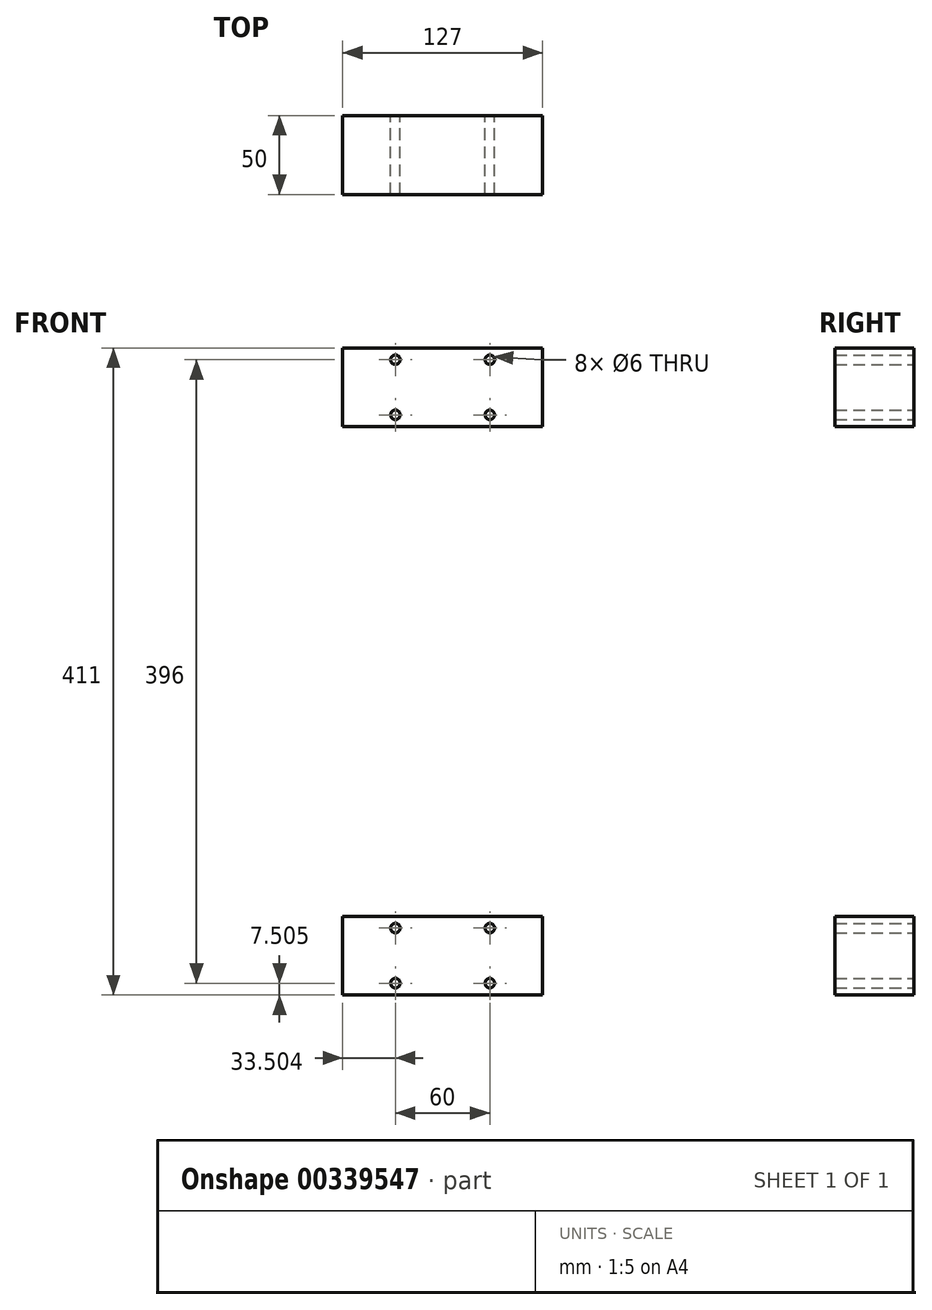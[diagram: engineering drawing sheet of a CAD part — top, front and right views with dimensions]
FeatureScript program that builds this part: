
annotation { "Feature Type Name" : "Feature", "Feature Type Description" : "" }
export const myFeature = defineFeature(function(context is Context, id is Id, definition is map)
    precondition{}
    {
        {
            var Q0;
            Q0=qCreatedBy(makeId("Front.planeOp"),FACE);
            var sketch = newSketch(context, id + "F0", { "sketchPlane" : qUnion([Q0])});
            skLineSegment(sketch, "E0.bottom", {"start": v(-64.23, 313.81) * mm, "end": v(62.77, 313.81) * mm});
            skLineSegment(sketch, "E0.top", {"start": v(-64.23, 263.81) * mm, "end": v(62.77, 263.81) * mm});
            skLineSegment(sketch, "E0.left", {"start": v(-64.23, 313.81) * mm, "end": v(-64.23, 263.81) * mm});
            skLineSegment(sketch, "E0.right", {"start": v(62.77, 313.81) * mm, "end": v(62.77, 263.81) * mm});
            skLineSegment(sketch, "E1", {"start": v(-64.23, 288.81) * mm, "end": v(62.77, 288.81) * mm, "construction": true});
            skLineSegment(sketch, "E2", {"start": v(-0.73, 313.81) * mm, "end": v(-0.73, 263.81) * mm, "construction": true});
            skCircle(sketch, "E3", {"center": v(-30.73, 306.31) * mm, "radius": 3 * mm});
            skCircle(sketch, "E4", {"center": v(-30.73, 271.31) * mm, "radius": 3 * mm});
            skCircle(sketch, "E5", {"center": v(29.27, 271.31) * mm, "radius": 3 * mm});
            skCircle(sketch, "E6", {"center": v(29.27, 306.31) * mm, "radius": 3 * mm});
            skLineSegment(sketch, "E7.bottom", {"start": v(-64.23, -47.19) * mm, "end": v(62.77, -47.19) * mm});
            skLineSegment(sketch, "E7.top", {"start": v(-64.23, -97.19) * mm, "end": v(62.77, -97.19) * mm});
            skLineSegment(sketch, "E7.left", {"start": v(-64.23, -47.19) * mm, "end": v(-64.23, -97.19) * mm});
            skLineSegment(sketch, "E7.right", {"start": v(62.77, -47.19) * mm, "end": v(62.77, -97.19) * mm});
            skLineSegment(sketch, "E8", {"start": v(-64.23, -72.19) * mm, "end": v(62.77, -72.19) * mm, "construction": true});
            skLineSegment(sketch, "E9", {"start": v(-0.73, -47.19) * mm, "end": v(-0.73, -97.19) * mm, "construction": true});
            skCircle(sketch, "E10", {"center": v(-30.73, -54.69) * mm, "radius": 3 * mm});
            skCircle(sketch, "E11", {"center": v(-30.73, -89.69) * mm, "radius": 3 * mm});
            skCircle(sketch, "E12", {"center": v(29.27, -89.69) * mm, "radius": 3 * mm});
            skCircle(sketch, "E13", {"center": v(29.27, -54.69) * mm, "radius": 3 * mm});
            skLineSegment(sketch, "E14", {"start": v(62.77, 313.81) * mm, "end": v(62.77, -97.19) * mm});
            skSolve(sketch);
        }
        {
            var Q0;
            Q0 = qSketchRegion(id + "F0", true);
            extrude(context, id + "F1", {"entities" : qUnion([Q0]), "depth" : 50 * mm});
        }
    });
